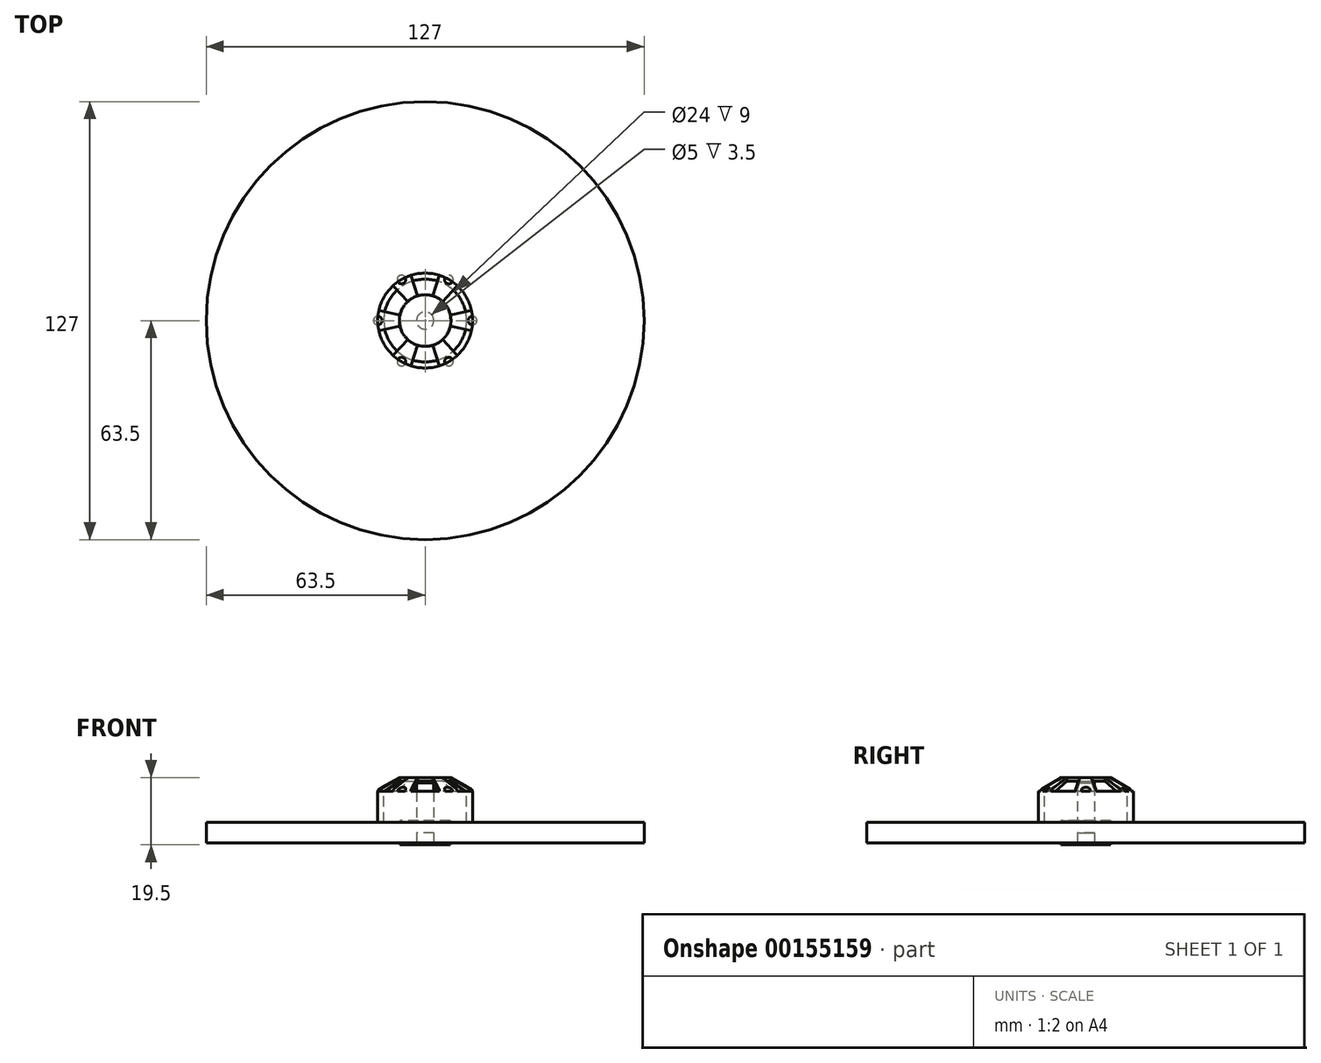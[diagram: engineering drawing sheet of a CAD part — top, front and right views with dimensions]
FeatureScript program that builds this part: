
annotation { "Feature Type Name" : "Feature", "Feature Type Description" : "" }
export const myFeature = defineFeature(function(context is Context, id is Id, definition is map)
    precondition{}
    {
        {
            var Q0;
            Q0=qCreatedBy(makeId("Top.planeOp"),FACE);
            var sketch = newSketch(context, id + "F0", { "sketchPlane" : qUnion([Q0])});
            skCircle(sketch, "E0", {"center": v(0, 0) * mm, "radius": 13.75 * mm});
            skSolve(sketch);
        }
        {
            var Q0;
            Q0 = qSketchRegion(id + "F0", true);
            extrude(context, id + "F1", {"entities" : qUnion([Q0]), "depth" : 16 * mm});
        }
        {
            var Q0;
            Q0=makeQuery(id+"F1.opExtrude","CAP_EDGE",EDGE,{"disambiguationData":[OSD([sQuery(id+"F0.wireOp",EDGE,"E0")])],"isStart":false});
            chamfer(context, id + "F2", {"entities" : qUnion([Q0]), "chamferType" : ChamferType.TWO_OFFSETS, "width1" : 6.25 * mm, "oppositeDirection" : false, "width2" : 3.5 * mm, "tangentPropagation" : true});
        }
        {
            var Q0;
            Q0=makeQuery(id+"F1.opExtrude","CAP_EDGE",EDGE,{"disambiguationData":[OSD([sQuery(id+"F0.wireOp",EDGE,"E0")])],"isStart":true});
            chamfer(context, id + "F3", {"entities" : qUnion([Q0]), "chamferType" : ChamferType.TWO_OFFSETS, "width1" : 3 * mm, "oppositeDirection" : false, "width2" : 2 * mm, "tangentPropagation" : true});
        }
        {
            var Q0;
            Q0=makeQuery(id+"F1.opExtrude","CAP_FACE",FACE,{"disambiguationData":[OSD([sQuery(id+"F0.wireOp",EDGE,"E0")])],"isStart":false});
            var sketch = newSketch(context, id + "F4", { "sketchPlane" : qUnion([Q0])});
            skArc(sketch, "E1", {"start": v(2.25, 7.15) * mm, "mid": v(0, 7.5) * mm, "end": v(-2.25, 7.15) * mm});
            skArc(sketch, "E2", {"start": v(4.13, 13.12) * mm, "mid": v(0, 13.75) * mm, "end": v(-4.13, 13.12) * mm});
            skLineSegment(sketch, "E3", {"start": v(0, 0) * mm, "end": v(-2.25, 7.15) * mm, "construction": true});
            skLineSegment(sketch, "E4", {"start": v(0, 0) * mm, "end": v(2.25, 7.15) * mm, "construction": true});
            skLineSegment(sketch, "E5", {"start": v(-2.25, 7.15) * mm, "end": v(-4.12, 13.12) * mm});
            skLineSegment(sketch, "E6", {"start": v(2.25, 7.15) * mm, "end": v(4.12, 13.12) * mm});
            skLineSegment(sketch, "E7.1.0", {"start": v(-5.07, 5.53) * mm, "end": v(-9.3, 10.13) * mm});
            skLineSegment(sketch, "E7.1.1", {"start": v(-7.32, 1.63) * mm, "end": v(-13.42, 2.99) * mm});
            skLineSegment(sketch, "E7.1.2", {"start": v(0, 0) * mm, "end": v(-7.32, 1.63) * mm, "construction": true});
            skLineSegment(sketch, "E7.1.3", {"start": v(0, 0) * mm, "end": v(-5.07, 5.53) * mm, "construction": true});
            skArc(sketch, "E7.1.4", {"start": v(-9.3, 10.13) * mm, "mid": v(-11.9, 6.88) * mm, "end": v(-13.42, 2.99) * mm});
            skArc(sketch, "E7.1.5", {"start": v(-5.07, 5.53) * mm, "mid": v(-6.5, 3.75) * mm, "end": v(-7.32, 1.63) * mm});
            skLineSegment(sketch, "E7.2.0", {"start": v(-7.32, -1.63) * mm, "end": v(-13.42, -2.99) * mm});
            skLineSegment(sketch, "E7.2.1", {"start": v(-5.07, -5.53) * mm, "end": v(-9.3, -10.13) * mm});
            skLineSegment(sketch, "E7.2.2", {"start": v(0, 0) * mm, "end": v(-5.07, -5.53) * mm, "construction": true});
            skLineSegment(sketch, "E7.2.3", {"start": v(0, 0) * mm, "end": v(-7.32, -1.63) * mm, "construction": true});
            skArc(sketch, "E7.2.4", {"start": v(-13.42, -2.99) * mm, "mid": v(-11.9, -6.87) * mm, "end": v(-9.3, -10.13) * mm});
            skArc(sketch, "E7.2.5", {"start": v(-7.32, -1.63) * mm, "mid": v(-6.5, -3.75) * mm, "end": v(-5.07, -5.53) * mm});
            skLineSegment(sketch, "E7.3.0", {"start": v(-2.25, -7.15) * mm, "end": v(-4.13, -13.12) * mm});
            skLineSegment(sketch, "E7.3.1", {"start": v(2.25, -7.15) * mm, "end": v(4.12, -13.12) * mm});
            skLineSegment(sketch, "E7.3.2", {"start": v(0, 0) * mm, "end": v(2.25, -7.15) * mm, "construction": true});
            skLineSegment(sketch, "E7.3.3", {"start": v(0, 0) * mm, "end": v(-2.25, -7.15) * mm, "construction": true});
            skArc(sketch, "E7.3.4", {"start": v(-4.13, -13.12) * mm, "mid": v(0, -13.75) * mm, "end": v(4.12, -13.12) * mm});
            skArc(sketch, "E7.3.5", {"start": v(-2.25, -7.15) * mm, "mid": v(0, -7.5) * mm, "end": v(2.25, -7.15) * mm});
            skLineSegment(sketch, "E7.4.0", {"start": v(5.07, -5.53) * mm, "end": v(9.3, -10.13) * mm});
            skLineSegment(sketch, "E7.4.1", {"start": v(7.32, -1.63) * mm, "end": v(13.42, -2.99) * mm});
            skLineSegment(sketch, "E7.4.2", {"start": v(0, 0) * mm, "end": v(7.32, -1.63) * mm, "construction": true});
            skLineSegment(sketch, "E7.4.3", {"start": v(0, 0) * mm, "end": v(5.07, -5.53) * mm, "construction": true});
            skArc(sketch, "E7.4.4", {"start": v(9.3, -10.13) * mm, "mid": v(11.9, -6.88) * mm, "end": v(13.42, -2.99) * mm});
            skArc(sketch, "E7.4.5", {"start": v(5.07, -5.53) * mm, "mid": v(6.5, -3.75) * mm, "end": v(7.32, -1.63) * mm});
            skLineSegment(sketch, "E7.5.0", {"start": v(7.32, 1.63) * mm, "end": v(13.42, 2.99) * mm});
            skLineSegment(sketch, "E7.5.1", {"start": v(5.07, 5.53) * mm, "end": v(9.3, 10.13) * mm});
            skLineSegment(sketch, "E7.5.2", {"start": v(0, 0) * mm, "end": v(5.07, 5.53) * mm, "construction": true});
            skLineSegment(sketch, "E7.5.3", {"start": v(0, 0) * mm, "end": v(7.32, 1.63) * mm, "construction": true});
            skArc(sketch, "E7.5.4", {"start": v(13.42, 2.99) * mm, "mid": v(11.9, 6.88) * mm, "end": v(9.3, 10.13) * mm});
            skArc(sketch, "E7.5.5", {"start": v(7.32, 1.63) * mm, "mid": v(6.5, 3.75) * mm, "end": v(5.07, 5.53) * mm});
            skSolve(sketch);
        }
        {
            var Q0;
            Q0 = qSketchRegion(id + "F4", true);
            extrude(context, id + "F5", {"entities" : qUnion([Q0]), "operationType" : NewBodyOperationType.REMOVE, "oppositeDirection" : true, "depth" : 4 * mm});
        }
        {
            var Q0;
            {var subQ0=sQuery(id+"F0.wireOp",EDGE,"E0");var subQ1=makeQuery(id+"F1.opExtrude","SWEPT_FACE",FACE,{"disambiguationData":[OSD([subQ0])]});Q0=makeQuery(id+"F5.boolean.opBoolean","SPLIT",EDGE,{"disambiguationData":[TD([makeQuery(id+"F5.opExtrude","SWEPT_FACE",FACE,{"disambiguationData":[OSD([sQuery(id+"F4.wireOp",EDGE,"E7.4.1")])]})])],"derivedFrom":makeQuery(id+"F2.opChamfer","BLEND_EDGE",EDGE,{"blendedFrom":[makeQuery(id+"F1.opExtrude","CAP_EDGE",EDGE,{"disambiguationData":[OSD([subQ0])],"isStart":false}),subQ1],"blendedInto":[subQ1]})});}
            var Q1;
            {var subQ0=sQuery(id+"F0.wireOp",EDGE,"E0");var subQ1=makeQuery(id+"F1.opExtrude","SWEPT_FACE",FACE,{"disambiguationData":[OSD([subQ0])]});Q1=makeQuery(id+"F5.boolean.opBoolean","SPLIT",EDGE,{"disambiguationData":[TD([makeQuery(id+"F5.opExtrude","SWEPT_FACE",FACE,{"disambiguationData":[OSD([sQuery(id+"F4.wireOp",EDGE,"E6")])]})])],"derivedFrom":makeQuery(id+"F2.opChamfer","BLEND_EDGE",EDGE,{"blendedFrom":[makeQuery(id+"F1.opExtrude","CAP_EDGE",EDGE,{"disambiguationData":[OSD([subQ0])],"isStart":false}),subQ1],"blendedInto":[subQ1]})});}
            var Q2;
            {var subQ0=sQuery(id+"F0.wireOp",EDGE,"E0");var subQ1=makeQuery(id+"F1.opExtrude","SWEPT_FACE",FACE,{"disambiguationData":[OSD([subQ0])]});Q2=makeQuery(id+"F5.boolean.opBoolean","SPLIT",EDGE,{"disambiguationData":[TD([makeQuery(id+"F5.opExtrude","SWEPT_FACE",FACE,{"disambiguationData":[OSD([sQuery(id+"F4.wireOp",EDGE,"E5")])]})])],"derivedFrom":makeQuery(id+"F2.opChamfer","BLEND_EDGE",EDGE,{"blendedFrom":[makeQuery(id+"F1.opExtrude","CAP_EDGE",EDGE,{"disambiguationData":[OSD([subQ0])],"isStart":false}),subQ1],"blendedInto":[subQ1]})});}
            var Q3;
            {var subQ0=sQuery(id+"F0.wireOp",EDGE,"E0");var subQ1=makeQuery(id+"F1.opExtrude","SWEPT_FACE",FACE,{"disambiguationData":[OSD([subQ0])]});Q3=makeQuery(id+"F5.boolean.opBoolean","SPLIT",EDGE,{"disambiguationData":[TD([makeQuery(id+"F5.opExtrude","SWEPT_FACE",FACE,{"disambiguationData":[OSD([sQuery(id+"F4.wireOp",EDGE,"E7.1.1")])]})])],"derivedFrom":makeQuery(id+"F2.opChamfer","BLEND_EDGE",EDGE,{"blendedFrom":[makeQuery(id+"F1.opExtrude","CAP_EDGE",EDGE,{"disambiguationData":[OSD([subQ0])],"isStart":false}),subQ1],"blendedInto":[subQ1]})});}
            var Q4;
            {var subQ0=sQuery(id+"F0.wireOp",EDGE,"E0");var subQ1=makeQuery(id+"F1.opExtrude","SWEPT_FACE",FACE,{"disambiguationData":[OSD([subQ0])]});Q4=makeQuery(id+"F5.boolean.opBoolean","SPLIT",EDGE,{"disambiguationData":[TD([makeQuery(id+"F5.opExtrude","SWEPT_FACE",FACE,{"disambiguationData":[OSD([sQuery(id+"F4.wireOp",EDGE,"E7.2.1")])]})])],"derivedFrom":makeQuery(id+"F2.opChamfer","BLEND_EDGE",EDGE,{"blendedFrom":[makeQuery(id+"F1.opExtrude","CAP_EDGE",EDGE,{"disambiguationData":[OSD([subQ0])],"isStart":false}),subQ1],"blendedInto":[subQ1]})});}
            var Q5;
            {var subQ0=sQuery(id+"F0.wireOp",EDGE,"E0");var subQ1=makeQuery(id+"F1.opExtrude","SWEPT_FACE",FACE,{"disambiguationData":[OSD([subQ0])]});Q5=makeQuery(id+"F5.boolean.opBoolean","SPLIT",EDGE,{"disambiguationData":[TD([makeQuery(id+"F5.opExtrude","SWEPT_FACE",FACE,{"disambiguationData":[OSD([sQuery(id+"F4.wireOp",EDGE,"E7.3.1")])]})])],"derivedFrom":makeQuery(id+"F2.opChamfer","BLEND_EDGE",EDGE,{"blendedFrom":[makeQuery(id+"F1.opExtrude","CAP_EDGE",EDGE,{"disambiguationData":[OSD([subQ0])],"isStart":false}),subQ1],"blendedInto":[subQ1]})});}
            fillet(context, id + "F6", {"entities" : qUnion([Q0, Q1, Q2, Q3, Q4, Q5]), "radius" : 0.75 * mm, "tangentPropagation" : true, "allowEdgeOverflow" : false});
        }
        {
            var Q0;
            Q0=makeQuery(id+"F1.opExtrude","CAP_FACE",FACE,{"disambiguationData":[OSD([sQuery(id+"F0.wireOp",EDGE,"E0")])],"isStart":false});
            var sketch = newSketch(context, id + "F7", { "sketchPlane" : qUnion([Q0])});
            skCircle(sketch, "E8", {"center": v(13.75, 0) * mm, "radius": 1.25 * mm});
            skCircle(sketch, "E9.1.0", {"center": v(6.88, 11.9) * mm, "radius": 1.25 * mm});
            skCircle(sketch, "E9.2.0", {"center": v(-6.87, 11.9) * mm, "radius": 1.25 * mm});
            skCircle(sketch, "E9.3.0", {"center": v(-13.75, 0) * mm, "radius": 1.25 * mm});
            skCircle(sketch, "E9.4.0", {"center": v(-6.88, -11.9) * mm, "radius": 1.25 * mm});
            skCircle(sketch, "E9.5.0", {"center": v(6.88, -11.9) * mm, "radius": 1.25 * mm});
            skPoint(sketch, "E9.center", {"position": v(0, 0) * mm});
            skSolve(sketch);
        }
        {
            var Q0;
            Q0 = qSketchRegion(id + "F7", true);
            extrude(context, id + "F8", {"entities" : qUnion([Q0]), "operationType" : NewBodyOperationType.REMOVE, "oppositeDirection" : true, "depth" : 4 * mm});
        }
        {
            var Q0;
            Q0=makeQuery(id+"F1.opExtrude","CAP_FACE",FACE,{"disambiguationData":[OSD([sQuery(id+"F0.wireOp",EDGE,"E0")])],"isStart":true});
            var sketch = newSketch(context, id + "F9", { "sketchPlane" : qUnion([Q0])});
            skArc(sketch, "E10", {"start": v(3, 10.84) * mm, "mid": v(0, 11.25) * mm, "end": v(-3, 10.84) * mm});
            skArc(sketch, "E11", {"start": v(3, 13.42) * mm, "mid": v(0, 13.75) * mm, "end": v(-3, 13.42) * mm});
            skLineSegment(sketch, "E12", {"start": v(-3, 13.42) * mm, "end": v(-3, 10.84) * mm});
            skLineSegment(sketch, "E13", {"start": v(3, 13.42) * mm, "end": v(3, 10.84) * mm});
            skLineSegment(sketch, "E14.1.0", {"start": v(-13.42, 3) * mm, "end": v(-10.84, 3) * mm});
            skArc(sketch, "E14.1.1", {"start": v(-13.42, 3) * mm, "mid": v(-13.75, 0) * mm, "end": v(-13.42, -3) * mm});
            skLineSegment(sketch, "E14.1.2", {"start": v(-13.42, -3) * mm, "end": v(-10.84, -3) * mm});
            skArc(sketch, "E14.1.3", {"start": v(-10.84, 3) * mm, "mid": v(-11.25, 0) * mm, "end": v(-10.84, -3) * mm});
            skLineSegment(sketch, "E14.2.0", {"start": v(-3, -13.42) * mm, "end": v(-3, -10.84) * mm});
            skArc(sketch, "E14.2.1", {"start": v(-3, -13.42) * mm, "mid": v(0, -13.75) * mm, "end": v(3, -13.42) * mm});
            skLineSegment(sketch, "E14.2.2", {"start": v(3, -13.42) * mm, "end": v(3, -10.84) * mm});
            skArc(sketch, "E14.2.3", {"start": v(-3, -10.84) * mm, "mid": v(0, -11.25) * mm, "end": v(3, -10.84) * mm});
            skLineSegment(sketch, "E14.3.0", {"start": v(13.42, -3) * mm, "end": v(10.84, -3) * mm});
            skArc(sketch, "E14.3.1", {"start": v(13.42, -3) * mm, "mid": v(13.75, 0) * mm, "end": v(13.42, 3) * mm});
            skLineSegment(sketch, "E14.3.2", {"start": v(13.42, 3) * mm, "end": v(10.84, 3) * mm});
            skArc(sketch, "E14.3.3", {"start": v(10.84, -3) * mm, "mid": v(11.25, 0) * mm, "end": v(10.84, 3) * mm});
            skSolve(sketch);
        }
        {
            var Q0;
            Q0 = qSketchRegion(id + "F9", true);
            extrude(context, id + "F10", {"entities" : qUnion([Q0]), "operationType" : NewBodyOperationType.REMOVE, "oppositeDirection" : true, "depth" : 2.8 * mm});
        }
        {
            var Q0;
            Q0=makeQuery(id+"F10.boolean.opBoolean","COPY",EDGE,{"derivedFrom":makeQuery(id+"F10.opExtrude","CAP_EDGE",EDGE,{"disambiguationData":[OSD([sQuery(id+"F9.wireOp",EDGE,"E10")])],"isStart":false})});
            var Q1;
            Q1=makeQuery(id+"F10.boolean.opBoolean","COPY",EDGE,{"derivedFrom":makeQuery(id+"F10.opExtrude","CAP_EDGE",EDGE,{"disambiguationData":[OSD([sQuery(id+"F9.wireOp",EDGE,"E14.1.3")])],"isStart":false})});
            var Q2;
            Q2=makeQuery(id+"F10.boolean.opBoolean","COPY",EDGE,{"derivedFrom":makeQuery(id+"F10.opExtrude","CAP_EDGE",EDGE,{"disambiguationData":[OSD([sQuery(id+"F9.wireOp",EDGE,"E14.2.3")])],"isStart":false})});
            var Q3;
            Q3=makeQuery(id+"F10.boolean.opBoolean","COPY",EDGE,{"derivedFrom":makeQuery(id+"F10.opExtrude","CAP_EDGE",EDGE,{"disambiguationData":[OSD([sQuery(id+"F9.wireOp",EDGE,"E14.3.3")])],"isStart":false})});
            chamfer(context, id + "F11", {"entities" : qUnion([Q0, Q1, Q2, Q3]), "chamferType" : ChamferType.TWO_OFFSETS, "width1" : 2.75 * mm, "oppositeDirection" : false, "width2" : 1.75 * mm, "tangentPropagation" : true});
        }
        {
            var Q0;
            Q0=qCreatedBy(makeId("Front.planeOp"),FACE);
            var sketch = newSketch(context, id + "F12", { "sketchPlane" : qUnion([Q0])});
            skLineSegment(sketch, "E15", {"start": v(0, 15) * mm, "end": v(-7.5, 15) * mm});
            skLineSegment(sketch, "E16", {"start": v(-7.5, 15) * mm, "end": v(-12, 12) * mm});
            skLineSegment(sketch, "E17", {"start": v(-12, 12) * mm, "end": v(-12, 3) * mm});
            skLineSegment(sketch, "E18", {"start": v(-12, 3) * mm, "end": v(-11, 1.5) * mm});
            skLineSegment(sketch, "E19", {"start": v(-11, 1.5) * mm, "end": v(0, 1.5) * mm});
            skLineSegment(sketch, "E20", {"start": v(0, 1.5) * mm, "end": v(0, 15) * mm});
            skSolve(sketch);
        }
        {
            var Q0;
            Q0 = qSketchRegion(id + "F12", true);
            var Q1;
            Q1=sQuery(id+"F12.wireOp",EDGE,"E20");
            revolve(context, id + "F13", {"operationType" : NewBodyOperationType.REMOVE, "entities" : qUnion([Q0]), "axis" : qUnion([Q1]), "revolveType" : RevolveType.FULL, "oppositeDirection" : true});
        }
        {
            var Q0;
            Q0=qCreatedBy(makeId("Top.planeOp"),FACE);
            var sketch = newSketch(context, id + "F14", { "sketchPlane" : qUnion([Q0])});
            skCircle(sketch, "E21", {"center": v(0, 0) * mm, "radius": 7.5 * mm});
            skSolve(sketch);
        }
        {
            var Q0;
            Q0=makeQuery(id+"F14.imprint","IMPRINT",FACE,{"disambiguationData":[TD([[makeQuery(id+"F14.imprint","IMPRINT",EDGE,{"derivedFrom":sQuery(id+"F14.wireOp",EDGE,"E21")}),1.0]])]});
            extrude(context, id + "F15", {"entities" : qUnion([Q0]), "depth" : 3 * mm});
        }
        {
            var Q0;
            Q0=makeQuery(id+"F15.opExtrude","CAP_FACE",FACE,{"disambiguationData":[OSD([sQuery(id+"F14.wireOp",EDGE,"E21")])],"isStart":false});
            var sketch = newSketch(context, id + "F16", { "sketchPlane" : qUnion([Q0])});
            skCircle(sketch, "E22", {"center": v(0, 0) * mm, "radius": 2.5 * mm});
            skSolve(sketch);
        }
        {
            var Q0;
            Q0=makeQuery(id+"F16.imprint","IMPRINT",FACE,{"disambiguationData":[TD([[makeQuery(id+"F16.imprint","IMPRINT",EDGE,{"derivedFrom":sQuery(id+"F16.wireOp",EDGE,"E22")}),1.0]])]});
            extrude(context, id + "F17", {"entities" : qUnion([Q0]), "operationType" : NewBodyOperationType.ADD, "depth" : 11.5 * mm});
        }
        {
            var Q0;
            Q0=qCreatedBy(makeId("Top.planeOp"),FACE);
            var sketch = newSketch(context, id + "F18", { "sketchPlane" : qUnion([Q0])});
            skCircle(sketch, "E23", {"center": v(0, 0) * mm, "radius": 7.25 * mm});
            skCircle(sketch, "E24", {"center": v(0, 0) * mm, "radius": 2.5 * mm});
            skSolve(sketch);
        }
        {
            var Q0;
            Q0=makeQuery(id+"F18.imprint","IMPRINT",FACE,{"disambiguationData":[TD([[makeQuery(id+"F18.imprint","IMPRINT",EDGE,{"derivedFrom":sQuery(id+"F18.wireOp",EDGE,"E23")}),1.0]])]});
            extrude(context, id + "F19", {"entities" : qUnion([Q0]), "endBound" : BoundingType.SYMMETRIC, "depth" : 7 * mm});
        }
        {
            var Q0;
            Q0=qCreatedBy(makeId("Top.planeOp"),FACE);
            var sketch = newSketch(context, id + "F20", { "sketchPlane" : qUnion([Q0])});
            skCircle(sketch, "E25", {"center": v(0, 0) * mm, "radius": 63.5 * mm});
            skCircle(sketch, "E26", {"center": v(0, 0) * mm, "radius": 7.25 * mm});
            skSolve(sketch);
        }
        {
            var Q0;
            Q0 = qSketchRegion(id + "F20", true);
            extrude(context, id + "F21", {"entities" : qUnion([Q0]), "operationType" : NewBodyOperationType.ADD, "endBound" : BoundingType.SYMMETRIC, "depth" : 6 * mm});
        }
    });
